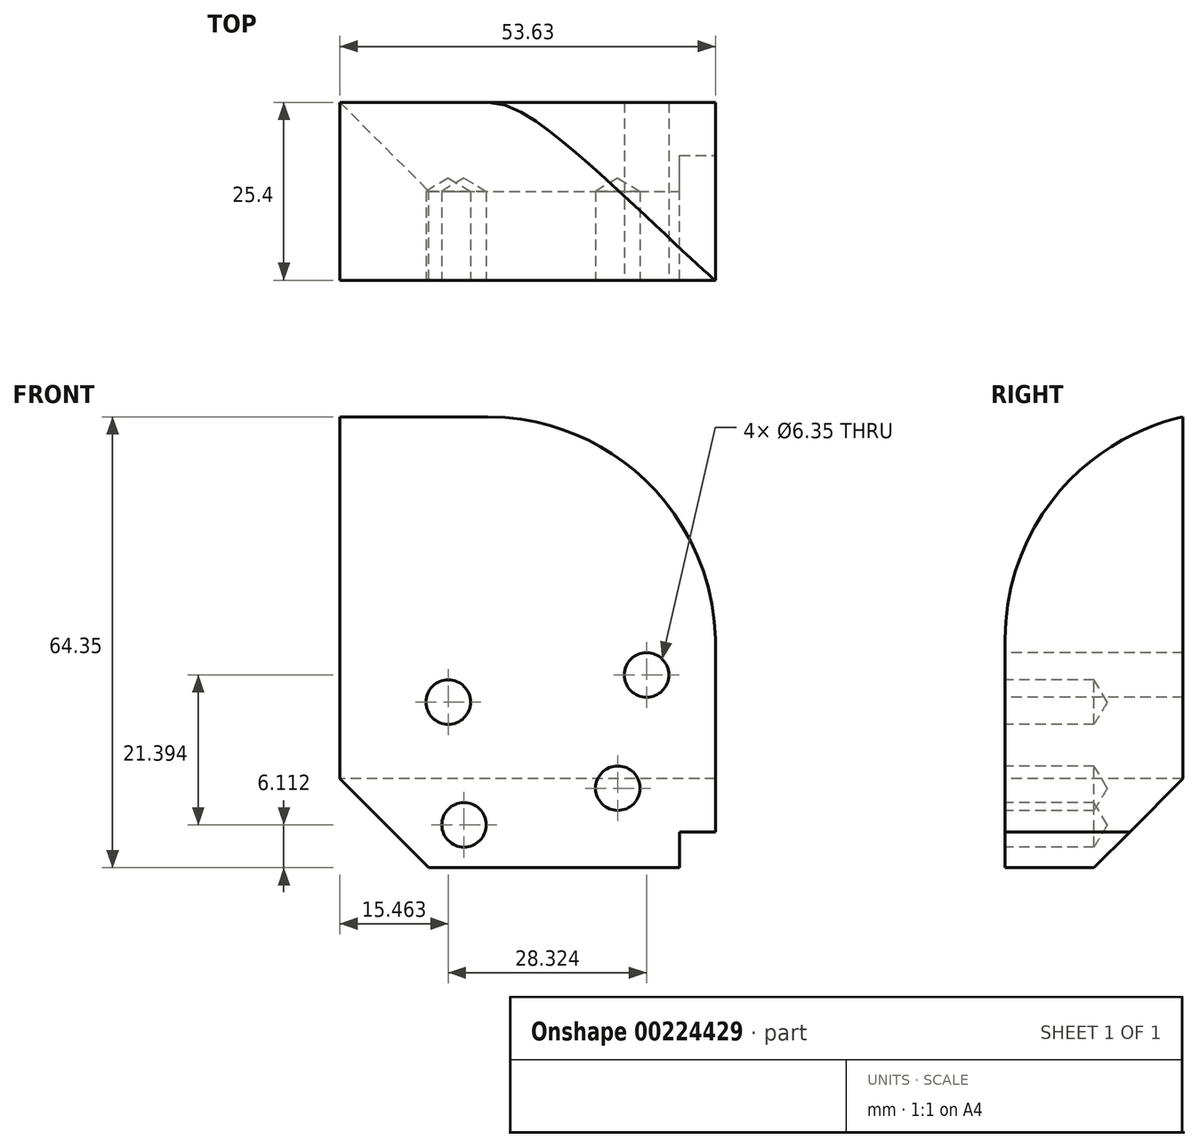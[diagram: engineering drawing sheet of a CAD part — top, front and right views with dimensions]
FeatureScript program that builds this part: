
annotation { "Feature Type Name" : "Feature", "Feature Type Description" : "" }
export const myFeature = defineFeature(function(context is Context, id is Id, definition is map)
    precondition{}
    {
        {
            var Q0;
            Q0=qCreatedBy(makeId("Front.planeOp"),FACE);
            var sketch = newSketch(context, id + "F0", { "sketchPlane" : qUnion([Q0])});
            skLineSegment(sketch, "E0.bottom", {"start": v(98.34, 35.93) * mm, "end": v(-98.34, 35.93) * mm});
            skLineSegment(sketch, "E0.top", {"start": v(98.34, -35.93) * mm, "end": v(-98.34, -35.93) * mm});
            skLineSegment(sketch, "E0.left", {"start": v(98.34, 35.93) * mm, "end": v(98.34, -35.93) * mm});
            skLineSegment(sketch, "E0.right", {"start": v(-98.34, 35.93) * mm, "end": v(-98.34, -35.93) * mm});
            skPoint(sketch, "E0.middle", {"position": v(0, 0) * mm});
            skLineSegment(sketch, "E1.bottom", {"start": v(-146.32, -16.68) * mm, "end": v(-74.3, -16.68) * mm});
            skLineSegment(sketch, "E1.top", {"start": v(-146.32, 16.68) * mm, "end": v(-74.3, 16.68) * mm});
            skLineSegment(sketch, "E1.left", {"start": v(-146.32, -16.68) * mm, "end": v(-146.32, 16.68) * mm});
            skLineSegment(sketch, "E1.right", {"start": v(-74.3, -16.68) * mm, "end": v(-74.3, 16.68) * mm});
            skPoint(sketch, "E1.middle", {"position": v(-110.31, 0) * mm});
            skLineSegment(sketch, "E2.bottom", {"start": v(-93.2, 30.83) * mm, "end": v(-146.83, 30.83) * mm});
            skLineSegment(sketch, "E2.top", {"start": v(-93.2, 95.18) * mm, "end": v(-146.83, 95.18) * mm});
            skLineSegment(sketch, "E2.left", {"start": v(-93.2, 30.83) * mm, "end": v(-93.2, 95.18) * mm});
            skLineSegment(sketch, "E2.right", {"start": v(-146.83, 30.83) * mm, "end": v(-146.83, 95.18) * mm});
            skPoint(sketch, "E2.middle", {"position": v(-120.02, 63) * mm});
            skSolve(sketch);
        }
        {
            var Q0;
            {var subQ6=sQuery(id+"F0.wireOp",EDGE,"E2.top");Q0=makeQuery(id+"F0.imprint","IMPRINT",FACE,{"disambiguationData":[TD([[makeQuery(id+"F0.imprint","IMPRINT",EDGE,{"derivedFrom":subQ6}),1.0]])]});}
            extrude(context, id + "F1", {"entities" : qUnion([Q0]), "depth" : 25.4 * mm, "offsetDistance" : 25.4 * mm});
        }
        {
            var Q0;
            Q0=makeQuery(id+"F1.opExtrude","SWEPT_EDGE",EDGE,{"disambiguationData":[OSD([sQuery(id+"F0.wireOp",EDGE,"E2.top"),sQuery(id+"F0.wireOp",EDGE,"E2.left")])]});
            var Q1;
            Q1=makeQuery(id+"F1.opExtrude","CAP_EDGE",EDGE,{"disambiguationData":[OSD([sQuery(id+"F0.wireOp",EDGE,"E2.top")])],"isStart":false});
            fillet(context, id + "F2", {"entities" : qUnion([Q0, Q1]), "radius" : 32.5 * mm, "tangentPropagation" : true, "allowEdgeOverflow" : false});
        }
        {
            var Q0;
            Q0=makeQuery(id+"F1.opExtrude","CAP_EDGE",EDGE,{"disambiguationData":[OSD([sQuery(id+"F0.wireOp",EDGE,"E2.bottom")])],"isStart":true});
            var Q1;
            Q1=makeQuery(id+"F1.opExtrude","SWEPT_EDGE",EDGE,{"disambiguationData":[OSD([sQuery(id+"F0.wireOp",EDGE,"E2.bottom"),sQuery(id+"F0.wireOp",EDGE,"E2.right")])]});
            chamfer(context, id + "F3", {"entities" : qUnion([Q0, Q1]), "width" : 12.7 * mm, "tangentPropagation" : true});
        }
        {
            var Q0;
            Q0=makeQuery(id+"F1.opExtrude","CAP_FACE",FACE,{"disambiguationData":[OSD([sQuery(id+"F0.wireOp",EDGE,"E0.bottom"),sQuery(id+"F0.wireOp",EDGE,"E0.right"),sQuery(id+"F0.wireOp",EDGE,"E2.bottom"),sQuery(id+"F0.wireOp",EDGE,"E2.top"),sQuery(id+"F0.wireOp",EDGE,"E2.left"),sQuery(id+"F0.wireOp",EDGE,"E2.right")])],"isStart":false});
            var sketch = newSketch(context, id + "F4", { "sketchPlane" : qUnion([Q0])});
            skLineSegment(sketch, "E3", {"start": v(-131.37, 54.46) * mm, "end": v(-107.15, 42.17) * mm});
            skLineSegment(sketch, "E4", {"start": v(-107.15, 42.17) * mm, "end": v(-103.04, 58.34) * mm});
            skLineSegment(sketch, "E5", {"start": v(-103.04, 58.34) * mm, "end": v(-129.1, 36.94) * mm});
            skLineSegment(sketch, "E6", {"start": v(-129.1, 36.94) * mm, "end": v(-133.3, 42.04) * mm});
            skSolve(sketch);
        }
        {
            var Q0;
            Q0=sQuery(id+"F4.wireOp",VERTEX,"E4.end");
            var Q1;
            Q1=makeQuery(id+"F1.opExtrude","SWEPT_BODY",BODY,{"disambiguationData":[OSD([sQuery(id+"F0.wireOp",EDGE,"E0.bottom"),sQuery(id+"F0.wireOp",EDGE,"E0.right"),sQuery(id+"F0.wireOp",EDGE,"E2.bottom"),sQuery(id+"F0.wireOp",EDGE,"E2.top"),sQuery(id+"F0.wireOp",EDGE,"E2.left"),sQuery(id+"F0.wireOp",EDGE,"E2.right")])]});
            hole(context, id + "F5", {"style" : HoleStyle.SIMPLE, "endStyle" : HoleEndStyle.THROUGH, "holeDiameter" : 6.35 * mm, "majorDiameter" : 6.35 * mm, "isTappedThrough" : true, "tappedDepth" : 12.7 * mm, "tapClearance" : 3, "locations" : qUnion([Q0]), "scope" : qUnion([Q1])});
        }
        {
            var Q0;
            Q0=sQuery(id+"F4.wireOp",VERTEX,"E3.start");
            var Q1;
            Q1=sQuery(id+"F4.wireOp",VERTEX,"E3.end");
            var Q2;
            Q2=sQuery(id+"F4.wireOp",VERTEX,"E5.end");
            var Q3;
            Q3=makeQuery(id+"F1.opExtrude","SWEPT_BODY",BODY,{"disambiguationData":[OSD([sQuery(id+"F0.wireOp",EDGE,"E0.bottom"),sQuery(id+"F0.wireOp",EDGE,"E0.right"),sQuery(id+"F0.wireOp",EDGE,"E2.bottom"),sQuery(id+"F0.wireOp",EDGE,"E2.top"),sQuery(id+"F0.wireOp",EDGE,"E2.left"),sQuery(id+"F0.wireOp",EDGE,"E2.right")])]});
            hole(context, id + "F6", {"style" : HoleStyle.SIMPLE, "endStyle" : HoleEndStyle.BLIND, "holeDiameter" : 6.35 * mm, "majorDiameter" : 6.35 * mm, "holeDepth" : 12.7 * mm, "isTappedThrough" : true, "tappedDepth" : 12.7 * mm, "tapClearance" : 3, "locations" : qUnion([Q0, Q1, Q2]), "scope" : qUnion([Q3])});
        }
    });
